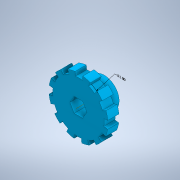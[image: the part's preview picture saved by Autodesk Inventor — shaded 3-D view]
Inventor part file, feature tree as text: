
AUTODESK INVENTOR PART (.ipt)
format: ipt  version: 2021.2 (Build 252289000, 289)  size: 177,152 bytes
history: native  units: in
note: dims shown in document units (in); Inventor stores cm internally (conversion verified against a paired STEP export)
features: extrude x4, other x3, sketch x2, pattern_circular x1
ambient origin geometry x8: Origin, YZ Plane, XZ Plane, XY Plane, X Axis, Y Axis, Z Axis, Center Point
bodies: Solid1 (feature_tree)
feature tree (10):
  other  "Annotations"
  extrude  "Extrusion1"  Depth=0.375in TaperAngle=0.0deg
  extrude  "Extrusion4"  Depth=1.0in
  pattern_circular  "Circular Pattern2"  [2 undecoded]
  extrude  "Extrusion5"  TaperAngle=0.0deg  [1 undecoded]
  extrude  "Extrusion2"  Depth=1.0in
  sketch  "Sketch1"  dims[d0=2.0in d1=0.375in d2=0.0in]
  sketch  "Sketch4"  dims[d6=0.25in d7=0.0in d17=0.1309in d18=0.375in d19=0.0in d20=4.7244in d21=360.0deg d23=0.5in d24=15.0deg d27=1.0in d28=0.5in d29=0.0in d25=0.3594in d26=1.0in d30=2.2038in d31=1.0in]
  other  "Radial Dimension 1"
  other  "Diameter Dimension 1"
note: 3 required parameter values undecoded (feature->parameter linkage not recoverable at this tier; creation-order binding heuristic only, values carry confidence <= 0.55)
